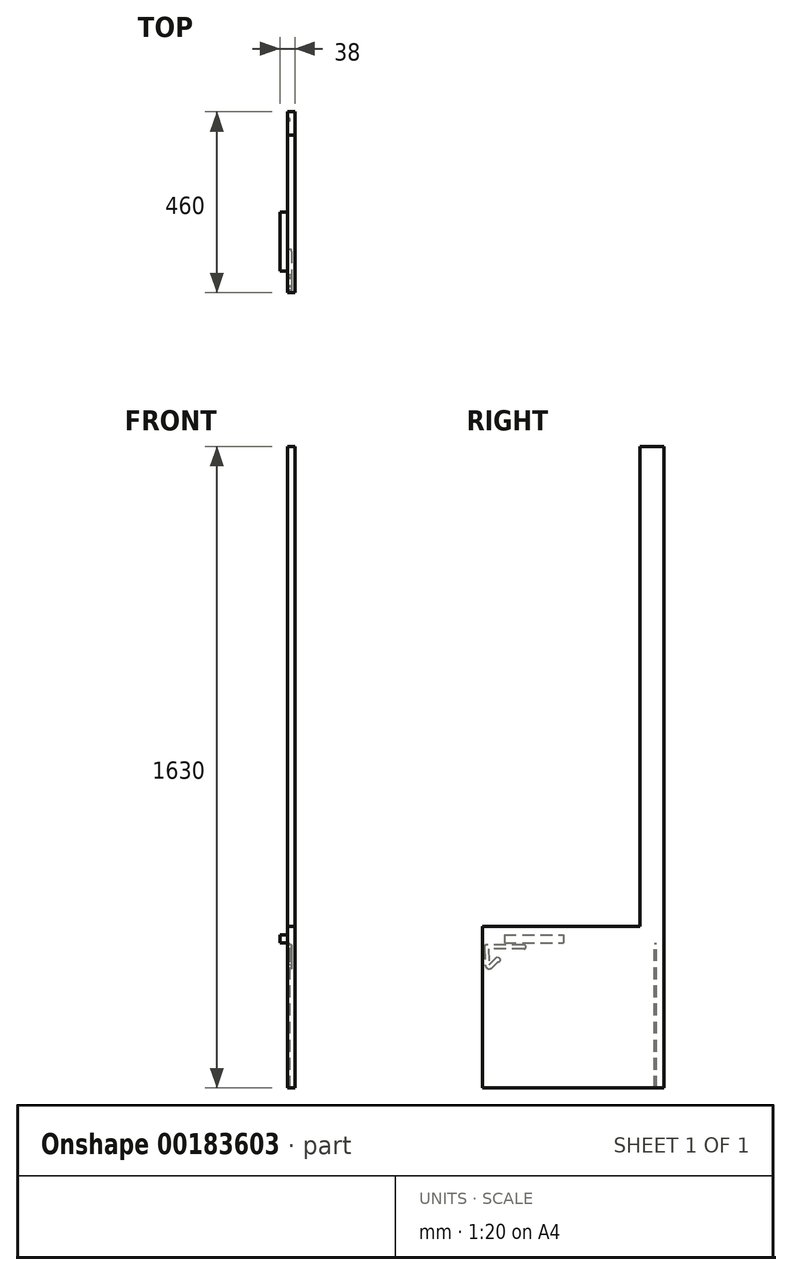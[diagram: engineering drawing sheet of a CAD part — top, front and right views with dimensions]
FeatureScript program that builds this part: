
annotation { "Feature Type Name" : "Feature", "Feature Type Description" : "" }
export const myFeature = defineFeature(function(context is Context, id is Id, definition is map)
    precondition{}
    {
        {
            var Q0;
            Q0=qCreatedBy(makeId("Right.planeOp"),FACE);
            var sketch = newSketch(context, id + "F0", { "sketchPlane" : qUnion([Q0])});
            skLineSegment(sketch, "E0.bottom", {"start": v(30, 722.5) * mm, "end": v(-30, 722.5) * mm});
            skLineSegment(sketch, "E0.left", {"start": v(30, 722.5) * mm, "end": v(30, -907.5) * mm});
            skLineSegment(sketch, "E0.right", {"start": v(-30, 722.5) * mm, "end": v(-30, -497.5) * mm});
            skPoint(sketch, "E0.middle", {"position": v(0, 0) * mm});
            skLineSegment(sketch, "E1", {"start": v(-430, -907.5) * mm, "end": v(-430, -497.5) * mm});
            skLineSegment(sketch, "E2", {"start": v(-430, -497.5) * mm, "end": v(-30, -497.5) * mm});
            skLineSegment(sketch, "E3", {"start": v(-430, -907.5) * mm, "end": v(30, -907.5) * mm});
            skSolve(sketch);
        }
        {
            var Q0;
            Q0 = qSketchRegion(id + "F0", true);
            extrude(context, id + "F1", {"entities" : qUnion([Q0]), "depth" : 18 * mm});
        }
        {
            var Q0;
            Q0=makeQuery(id+"F1.opExtrude","CAP_FACE",FACE,{"disambiguationData":[OSD([sQuery(id+"F0.wireOp",EDGE,"E0.bottom"),sQuery(id+"F0.wireOp",EDGE,"E0.left"),sQuery(id+"F0.wireOp",EDGE,"E0.right"),sQuery(id+"F0.wireOp",EDGE,"E1"),sQuery(id+"F0.wireOp",EDGE,"E2"),sQuery(id+"F0.wireOp",EDGE,"E3")])],"isStart":true});
            var sketch = newSketch(context, id + "F2", { "sketchPlane" : qUnion([Q0])});
            skLineSegment(sketch, "E4.bottom", {"start": v(-12, -907.5) * mm, "end": v(-6, -907.5) * mm});
            skLineSegment(sketch, "E4.top", {"start": v(-12, -541.5) * mm, "end": v(-6, -541.5) * mm});
            skLineSegment(sketch, "E4.left", {"start": v(-12, -907.5) * mm, "end": v(-12, -541.5) * mm});
            skLineSegment(sketch, "E4.right", {"start": v(-6, -907.5) * mm, "end": v(-6, -541.5) * mm});
            skSolve(sketch);
        }
        {
            var Q0;
            Q0 = qSketchRegion(id + "F2", true);
            extrude(context, id + "F3", {"entities" : qUnion([Q0]), "operationType" : NewBodyOperationType.REMOVE, "oppositeDirection" : true, "depth" : 6 * mm});
        }
        {
            var Q0;
            Q0=makeQuery(id+"F1.opExtrude","CAP_FACE",FACE,{"disambiguationData":[OSD([sQuery(id+"F0.wireOp",EDGE,"E0.bottom"),sQuery(id+"F0.wireOp",EDGE,"E0.left"),sQuery(id+"F0.wireOp",EDGE,"E0.right"),sQuery(id+"F0.wireOp",EDGE,"E1"),sQuery(id+"F0.wireOp",EDGE,"E2"),sQuery(id+"F0.wireOp",EDGE,"E3")])],"isStart":true});
            var sketch = newSketch(context, id + "F4", { "sketchPlane" : qUnion([Q0])});
            skLineSegment(sketch, "E5.0", {"start": v(410, -517.5) * mm, "end": v(30, -517.5) * mm, "construction": true});
            skLineSegment(sketch, "E5.1", {"start": v(410, -912.5) * mm, "end": v(410, -517.5) * mm, "construction": true});
            skLineSegment(sketch, "E6", {"start": v(410, -517.5) * mm, "end": v(430, -497.5) * mm, "construction": true});
            skLineSegment(sketch, "E7", {"start": v(212.36, -549.5) * mm, "end": v(420, -549.5) * mm, "construction": true});
            skLineSegment(sketch, "E8", {"start": v(390, -582.5) * mm, "end": v(390, -604.5) * mm, "construction": true});
            skLineSegment(sketch, "E9", {"start": v(390, -604.5) * mm, "end": v(412, -604.5) * mm, "construction": true});
            skLineSegment(sketch, "E10", {"start": v(390, -582.5) * mm, "end": v(404.81, -582.5) * mm, "construction": true});
            skLineSegment(sketch, "E11", {"start": v(390, -582.5) * mm, "end": v(391.88, -582) * mm, "construction": true});
            skLineSegment(sketch, "E12", {"start": v(393.81, -582.51) * mm, "end": v(410, -598.7) * mm, "construction": true});
            skLineSegment(sketch, "E13", {"start": v(420.1, -550.65) * mm, "end": v(418.53, -595.34) * mm, "construction": true});
            skPoint(sketch, "E14.visualSharp", {"position": v(418.13, -606.83) * mm});
            skArc(sketch, "E14.filletArc", {"start": v(410, -598.7) * mm, "mid": v(415.37, -599.82) * mm, "end": v(418.53, -595.34) * mm, "construction": true});
            skPoint(sketch, "E15.visualSharp", {"position": v(420.65, -534.65) * mm});
            skArc(sketch, "E15.filletArc", {"start": v(420.1, -550.65) * mm, "mid": v(420.08, -550.07) * mm, "end": v(420, -549.5) * mm, "construction": true});
            skArc(sketch, "E16.filletArc", {"start": v(412.19, -549.51) * mm, "mid": v(412, -549.5) * mm, "end": v(411.82, -549.5) * mm, "construction": true});
            skPoint(sketch, "E17.visualSharp", {"position": v(412.34, -581.34) * mm});
            skPoint(sketch, "E18.visualSharp", {"position": v(393, -581.7) * mm});
            skArc(sketch, "E18.filletArc", {"start": v(393.81, -582.51) * mm, "mid": v(392.91, -582) * mm, "end": v(391.88, -582) * mm, "construction": true});
            skLineSegment(sketch, "E19.2", {"start": v(-25, -902.5) * mm, "end": v(-17, -902.5) * mm});
            skArc(sketch, "E20.0", {"start": v(417.2, -560.25) * mm, "mid": v(417.26, -560.24) * mm, "end": v(417.32, -560.23) * mm});
            skArc(sketch, "E21", {"start": v(388.7, -577.67) * mm, "mid": v(385.17, -583.8) * mm, "end": v(391.3, -587.33) * mm});
            skArc(sketch, "E22", {"start": v(325, -544.5) * mm, "mid": v(320, -549.5) * mm, "end": v(325, -554.5) * mm});
            skLineSegment(sketch, "E23.0", {"start": v(325, -544.5) * mm, "end": v(423.11, -544.5) * mm});
            skArc(sketch, "E23.1", {"start": v(425.1, -550.83) * mm, "mid": v(424.64, -547.5) * mm, "end": v(423.11, -544.5) * mm});
            skLineSegment(sketch, "E23.2", {"start": v(391.3, -587.33) * mm, "end": v(391.5, -587.27) * mm});
            skLineSegment(sketch, "E23.3", {"start": v(391.5, -587.27) * mm, "end": v(406.46, -602.24) * mm, "construction": true});
            skArc(sketch, "E23.4", {"start": v(406.46, -602.24) * mm, "mid": v(417.2, -604.47) * mm, "end": v(423.53, -595.52) * mm});
            skLineSegment(sketch, "E23.5", {"start": v(425.1, -550.83) * mm, "end": v(423.53, -595.52) * mm, "construction": true});
            skLineSegment(sketch, "E24.0", {"start": v(212.36, -544.5) * mm, "end": v(423.11, -544.5) * mm, "construction": true});
            skArc(sketch, "E24.1", {"start": v(425.1, -550.83) * mm, "mid": v(424.64, -547.5) * mm, "end": v(423.11, -544.5) * mm, "construction": true});
            skLineSegment(sketch, "E24.2", {"start": v(391.3, -587.33) * mm, "end": v(391.5, -587.27) * mm, "construction": true});
            skLineSegment(sketch, "E24.3", {"start": v(391.5, -587.27) * mm, "end": v(406.46, -602.24) * mm});
            skArc(sketch, "E24.4", {"start": v(406.46, -602.24) * mm, "mid": v(417.2, -604.47) * mm, "end": v(423.53, -595.52) * mm, "construction": true});
            skLineSegment(sketch, "E24.5", {"start": v(425.1, -550.83) * mm, "end": v(423.53, -595.52) * mm});
            skLineSegment(sketch, "E25.0", {"start": v(394.49, -576.12) * mm, "end": v(413.54, -595.17) * mm});
            skLineSegment(sketch, "E25.1", {"start": v(388.7, -577.67) * mm, "end": v(394.49, -576.12) * mm});
            skLineSegment(sketch, "E26.0", {"start": v(414.96, -554.5) * mm, "end": v(413.54, -595.17) * mm});
            skLineSegment(sketch, "E26.1", {"start": v(325, -554.5) * mm, "end": v(414.96, -554.5) * mm});
            skSolve(sketch);
        }
        {
            var Q0;
            Q0 = qSketchRegion(id + "F4", true);
            extrude(context, id + "F5", {"entities" : qUnion([Q0]), "operationType" : NewBodyOperationType.REMOVE, "oppositeDirection" : true, "depth" : 10 * mm});
        }
        {
            var Q0;
            Q0=makeQuery(id+"F1.opExtrude","CAP_FACE",FACE,{"disambiguationData":[OSD([sQuery(id+"F0.wireOp",EDGE,"E0.bottom"),sQuery(id+"F0.wireOp",EDGE,"E0.left"),sQuery(id+"F0.wireOp",EDGE,"E0.right"),sQuery(id+"F0.wireOp",EDGE,"E1"),sQuery(id+"F0.wireOp",EDGE,"E2"),sQuery(id+"F0.wireOp",EDGE,"E3")])],"isStart":true});
            var sketch = newSketch(context, id + "F6", { "sketchPlane" : qUnion([Q0])});
            skLineSegment(sketch, "E27.bottom", {"start": v(375, -519.5) * mm, "end": v(225, -519.5) * mm});
            skLineSegment(sketch, "E27.top", {"start": v(375, -539.5) * mm, "end": v(225, -539.5) * mm});
            skLineSegment(sketch, "E27.left", {"start": v(375, -519.5) * mm, "end": v(375, -539.5) * mm});
            skLineSegment(sketch, "E27.right", {"start": v(225, -519.5) * mm, "end": v(225, -539.5) * mm});
            skPoint(sketch, "E27.middle", {"position": v(300, -529.5) * mm});
            skSolve(sketch);
        }
        {
            var Q0;
            Q0 = qSketchRegion(id + "F6", true);
            extrude(context, id + "F7", {"entities" : qUnion([Q0]), "operationType" : NewBodyOperationType.ADD, "depth" : 20 * mm});
        }
    });
